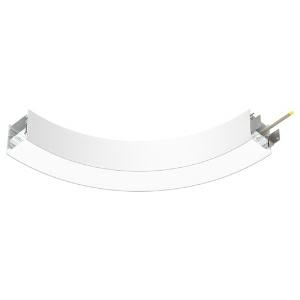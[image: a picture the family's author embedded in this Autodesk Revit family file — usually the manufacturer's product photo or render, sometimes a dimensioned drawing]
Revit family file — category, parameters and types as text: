
# Revit family: super-g_slim_super_g_slim_800_90deg_ab_ps_led__12w_1580lm_3000k_cri_80_350-1360_cc02
name_source: partatom
category: Leuchten
revit_build: Autodesk Revit 2016 (Build: 20190508_0715(x64)
units: mm (PartAtom-declared; Revit-internal decimal feet)

## family parameters
Basisbauteil = Fläche
Beim Laden mit Abzugskörper schneiden = Nein
Bemaßung runder Anschluss = Durchmesser verwenden
Gemeinsam genutzt = Nein
Lichtquelle = Nein
Raumberechnungspunkt = Nein
Teiletyp = Normal

## types (1)
- 350-1360-D01 (1 x LED, 480 lm, 3000K)
    Approval mark = CE
    Beschreibung = The insert consists of aluminum-extruded profile. Charming SOFT-EDGE design ensure unparalleled styling. The ballast is integrated and allows for an operation with 220-240V (50/60Hz). SUPER-G SLIM (# 350-1360) ist not dimmable (on/off).
    CIE Flux Codes = 48 79 96 100 71
    Color Rendering = 1B/80…89
    Color Temperature = 3000K
    Height = 90 mm
    Hersteller = Prolicht
    Lamp Light Flux = 480 lm
    Lamp count = 1
    Lampe = 1 x LED
    Length = 144 mm
    Luminous efficacy = 103 lm/W
    ModVariant = Nein
    Modell = 350-1360
    Mounting Place = Ceiling
    Mounting Type = Surface mounted
    Number of Poles = 1
    OnlyDefault = Ja
    Power Factor = 1
    Product Name = SUPER-G SLIM__SUPER G SLIM 800/90° AB PS LED: 12W 1580lm 3000K CRI:80
    Product group = Surface profile systems
    ProductGroupID = 335
    Protection Class = Protection class I
    Protection Degree = IP 20
    RLX_Detail_Level = 1
    RlxData = <blob elided: 40013 chars, md5=a7ca09c1>
    Scheinlast = 13 VA
    Socket = socket
    Standby Power = 0 W
    System Light Flux = 1361 lm
    System Power = 13 W
    Typenbild = 350-1360.jpg
    URL = http://relux.com
    VarID = 350-1360-d01
    Voltage = 0 V
    Vorgabe-Ansicht = 1800 mm
    Weight = 0.00 kg
    Width = 65 mm

## geometry (parser evidence)
native form markers: Sweep x22
no freeform markers — native parametric forms only
